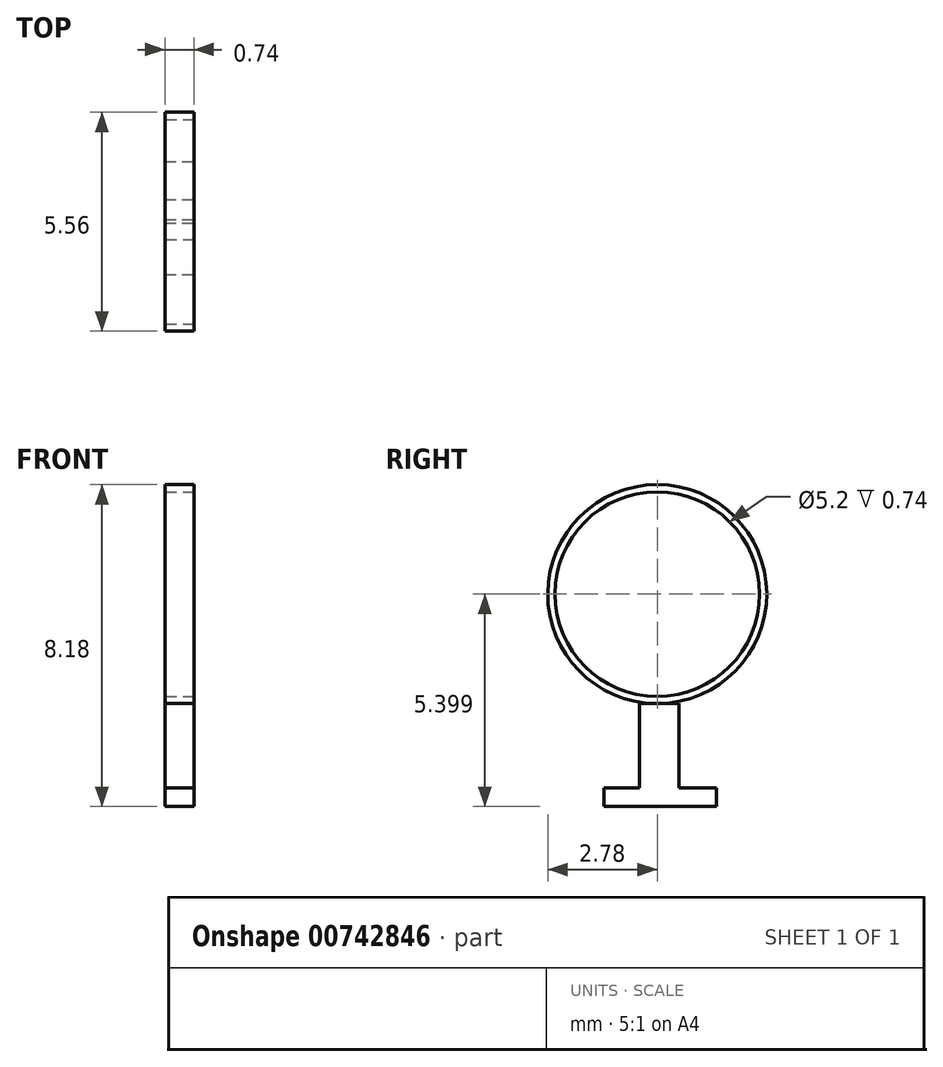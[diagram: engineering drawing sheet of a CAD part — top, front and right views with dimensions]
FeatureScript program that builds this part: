
annotation { "Feature Type Name" : "Feature", "Feature Type Description" : "" }
export const myFeature = defineFeature(function(context is Context, id is Id, definition is map)
    precondition{}
    {
        {
            var Q0;
            Q0=qCreatedBy(makeId("Front.planeOp"),FACE);
            var sketch = newSketch(context, id + "F0", { "sketchPlane" : qUnion([Q0])});
            skLineSegment(sketch, "E0.bottom", {"start": v(0.37, 1.3) * mm, "end": v(-0.37, 1.3) * mm});
            skLineSegment(sketch, "E0.top", {"start": v(0.37, -1.3) * mm, "end": v(-0.37, -1.3) * mm});
            skLineSegment(sketch, "E0.left", {"start": v(0.37, 1.3) * mm, "end": v(0.37, -1.3) * mm});
            skLineSegment(sketch, "E0.right", {"start": v(-0.37, 1.3) * mm, "end": v(-0.37, -1.3) * mm});
            skPoint(sketch, "E0.middle", {"position": v(0, 0) * mm});
            skSolve(sketch);
        }
        {
            var Q0;
            Q0=makeQuery(id+"F0.imprint","IMPRINT",FACE,{"disambiguationData":[TD([[makeQuery(id+"F0.imprint","IMPRINT",EDGE,{"derivedFrom":sQuery(id+"F0.wireOp",EDGE,"E0.bottom")}),1.0]])]});
            extrude(context, id + "F1", {"entities" : qUnion([Q0]), "depth" : 1 * mm, "offsetDistance" : 25 * mm});
        }
        {
            var Q0;
            Q0=makeQuery(id+"F1.opExtrude","CAP_FACE",FACE,{"disambiguationData":[OSD([sQuery(id+"F0.wireOp",EDGE,"E0.bottom"),sQuery(id+"F0.wireOp",EDGE,"E0.top"),sQuery(id+"F0.wireOp",EDGE,"E0.left"),sQuery(id+"F0.wireOp",EDGE,"E0.right")])],"isStart":true});
            var sketch = newSketch(context, id + "F2", { "sketchPlane" : qUnion([Q0])});
            skLineSegment(sketch, "E1.bottom", {"start": v(0.37, -1.3) * mm, "end": v(-0.37, -1.3) * mm});
            skLineSegment(sketch, "E1.top", {"start": v(0.37, -0.84) * mm, "end": v(-0.37, -0.84) * mm});
            skLineSegment(sketch, "E1.left", {"start": v(0.37, -1.3) * mm, "end": v(0.37, -0.84) * mm});
            skLineSegment(sketch, "E1.right", {"start": v(-0.37, -1.3) * mm, "end": v(-0.37, -0.84) * mm});
            skSolve(sketch);
        }
        {
            var Q0;
            Q0=makeQuery(id+"F2.imprint","IMPRINT",FACE,{"disambiguationData":[TD([[makeQuery(id+"F2.imprint","IMPRINT",EDGE,{"derivedFrom":sQuery(id+"F2.wireOp",EDGE,"E1.bottom")}),1.0]])]});
            var sketch = newSketch(context, id + "F3", { "sketchPlane" : qUnion([Q0])});
            skSolve(sketch);
        }
        {
            var Q0;
            Q0 = qSketchRegion(id + "F3", true);
            var Q1;
            Q1=makeQuery(id+"F3.imprint","IMPRINT",FACE,{"disambiguationData":[TD([[makeQuery(id+"F3.imprint","IMPRINT",EDGE,{"derivedFrom":makeQuery(id+"F2.imprint","IMPRINT",EDGE,{"derivedFrom":sQuery(id+"F2.wireOp",EDGE,"E1.bottom")})}),1.0]])]});
            extrude(context, id + "F4", {"entities" : qUnion([Q0, Q1]), "operationType" : NewBodyOperationType.ADD, "depth" : 0.96 * mm, "offsetDistance" : 25 * mm, "hasSecondDirection" : true, "secondDirectionOppositeDirection" : true, "secondDirectionDepth" : 1.9 * mm});
        }
        {
            var Q0;
            Q0=qCreatedBy(makeId("Right.planeOp"),FACE);
            var sketch = newSketch(context, id + "F5", { "sketchPlane" : qUnion([Q0])});
            skCircle(sketch, "E2", {"center": v(-0.52, 3.83) * mm, "radius": 2.52 * mm});
            skPoint(sketch, "E2.first.point", {"position": v(-0.5, 1.3) * mm});
            skPoint(sketch, "E2.second.point", {"position": v(-0.53, 6.36) * mm});
            skPoint(sketch, "E2.third.point", {"position": v(-2.05, 5.84) * mm});
            skSolve(sketch);
        }
        {
            var Q0;
            Q0=makeQuery(id+"F5.imprint","IMPRINT",FACE,{"disambiguationData":[TD([[makeQuery(id+"F5.imprint","IMPRINT",EDGE,{"derivedFrom":sQuery(id+"F5.wireOp",EDGE,"E2")}),1.0]])]});
            extrude(context, id + "F6", {"entities" : qUnion([Q0]), "operationType" : NewBodyOperationType.REMOVE, "oppositeDirection" : true, "depth" : .37 * mm, "offsetDistance" : 25 * mm, "hasSecondDirection" : true, "secondDirectionOppositeDirection" : false, "secondDirectionDepth" : .37 * mm});
        }
        {
            var Q0;
            Q0=qCreatedBy(makeId("Right.planeOp"),FACE);
            var sketch = newSketch(context, id + "F7", { "sketchPlane" : qUnion([Q0])});
            skCircle(sketch, "E3", {"center": v(-0.55, 4.09) * mm, "radius": 2.78 * mm});
            skPoint(sketch, "E3.first.point", {"position": v(-0.5, 1.3) * mm});
            skPoint(sketch, "E3.second.point", {"position": v(-0.42, 6.87) * mm});
            skPoint(sketch, "E3.third.point", {"position": v(-3, 5.4) * mm});
            skSolve(sketch);
        }
        {
            var Q0;
            Q0=makeQuery(id+"F7.imprint","IMPRINT",FACE,{"disambiguationData":[TD([[makeQuery(id+"F7.imprint","IMPRINT",EDGE,{"derivedFrom":sQuery(id+"F7.wireOp",EDGE,"E3")}),1.0]])]});
            extrude(context, id + "F8", {"entities" : qUnion([Q0]), "operationType" : NewBodyOperationType.ADD, "endBound" : BoundingType.SYMMETRIC, "depth" : 0.74 * mm, "offsetDistance" : 25 * mm});
        }
        {
            var Q0;
            Q0=makeQuery(id+"F8.opExtrude","CAP_FACE",FACE,{"disambiguationData":[OSD([sQuery(id+"F7.wireOp",EDGE,"E3")])],"isStart":false});
            var sketch = newSketch(context, id + "F9", { "sketchPlane" : qUnion([Q0])});
            skCircle(sketch, "E4", {"center": v(-0.55, 4.09) * mm, "radius": 2.6 * mm});
            skSolve(sketch);
        }
        {
            var Q0;
            Q0 = qSketchRegion(id + "F9", true);
            extrude(context, id + "F10", {"entities" : qUnion([Q0]), "operationType" : NewBodyOperationType.REMOVE, "oppositeDirection" : true, "depth" : 2.5 * mm, "offsetDistance" : 25 * mm});
        }
    });
